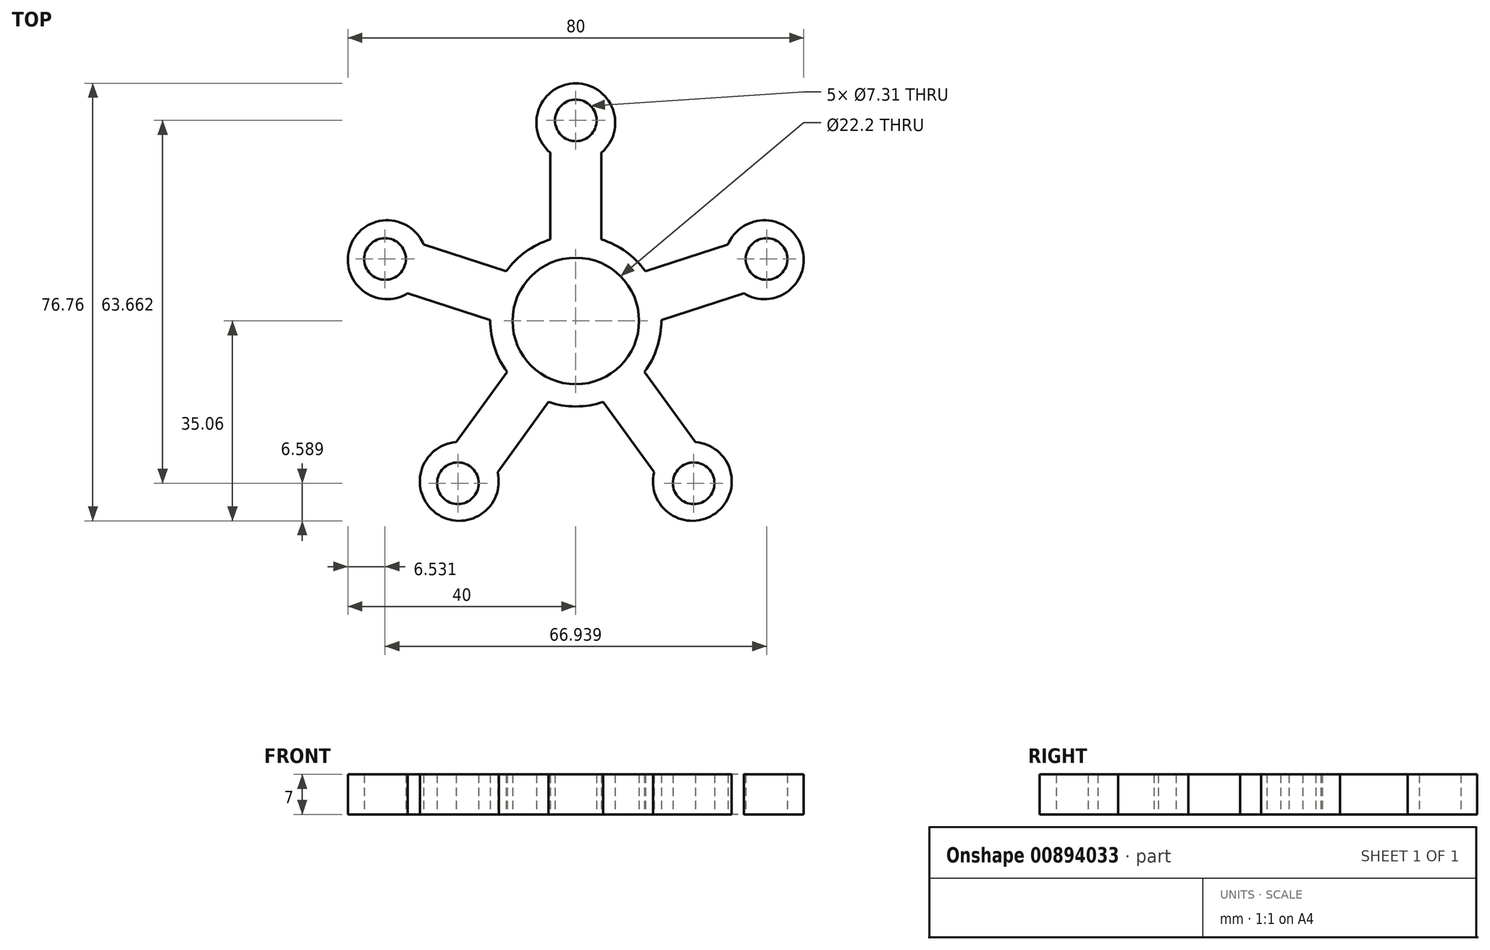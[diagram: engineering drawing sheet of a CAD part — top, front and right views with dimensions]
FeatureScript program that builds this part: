
annotation { "Feature Type Name" : "Feature", "Feature Type Description" : "" }
export const myFeature = defineFeature(function(context is Context, id is Id, definition is map)
    precondition{}
    {
        {
            var Q0;
            Q0=qCreatedBy(makeId("Top.planeOp"),FACE);
            var sketch = newSketch(context, id + "F0", { "sketchPlane" : qUnion([Q0])});
            skCircle(sketch, "E0", {"center": v(0, 0) * mm, "radius": 11.1 * mm});
            skSolve(sketch);
        }
        {
            var Q0;
            Q0=qCreatedBy(makeId("Top.planeOp"),FACE);
            var sketch = newSketch(context, id + "F1", { "sketchPlane" : qUnion([Q0])});
            skArc(sketch, "E1", {"start": v(-4.5, 14.3) * mm, "mid": v(-8.82, 12.14) * mm, "end": v(-12.22, 8.7) * mm});
            skLineSegment(sketch, "E2", {"start": v(-4.5, 14.3) * mm, "end": v(-4.5, 29.53) * mm});
            skLineSegment(sketch, "E3.MirrorCS", {"start": v(4.5, 14.3) * mm, "end": v(4.5, 29.53) * mm});
            skArc(sketch, "E4", {"start": v(4.5, 29.53) * mm, "mid": v(0, 41.7) * mm, "end": v(-4.5, 29.53) * mm});
            skPoint(sketch, "E4.third.point", {"position": v(4.5, 40.04) * mm});
            skArc(sketch, "E5.1.0", {"start": v(-26.7, 13.4) * mm, "mid": v(-39.66, 12.89) * mm, "end": v(-29.47, 4.85) * mm});
            skLineSegment(sketch, "E5.1.1", {"start": v(-12.22, 8.7) * mm, "end": v(-26.7, 13.4) * mm});
            skLineSegment(sketch, "E5.1.2", {"start": v(-15, 0.14) * mm, "end": v(-29.47, 4.85) * mm});
            skArc(sketch, "E5.2.0", {"start": v(-21, -21.24) * mm, "mid": v(-24.51, -33.74) * mm, "end": v(-13.72, -26.53) * mm});
            skLineSegment(sketch, "E5.2.1", {"start": v(-12.05, -8.93) * mm, "end": v(-21, -21.24) * mm});
            skLineSegment(sketch, "E5.2.2", {"start": v(-4.77, -14.22) * mm, "end": v(-13.72, -26.53) * mm});
            skArc(sketch, "E5.3.0", {"start": v(13.72, -26.53) * mm, "mid": v(24.51, -33.74) * mm, "end": v(21, -21.24) * mm});
            skLineSegment(sketch, "E5.3.1", {"start": v(4.77, -14.22) * mm, "end": v(13.72, -26.53) * mm});
            skLineSegment(sketch, "E5.3.2", {"start": v(12.05, -8.93) * mm, "end": v(21, -21.24) * mm});
            skArc(sketch, "E5.4.0", {"start": v(29.47, 4.85) * mm, "mid": v(39.66, 12.89) * mm, "end": v(26.7, 13.4) * mm});
            skLineSegment(sketch, "E5.4.1", {"start": v(15, 0.14) * mm, "end": v(29.47, 4.85) * mm});
            skLineSegment(sketch, "E5.4.2", {"start": v(12.22, 8.7) * mm, "end": v(26.7, 13.4) * mm});
            skArc(sketch, "E6.trimOffspring", {"start": v(12.22, 8.7) * mm, "mid": v(8.82, 12.14) * mm, "end": v(4.5, 14.3) * mm});
            skArc(sketch, "E7.trimOffspring", {"start": v(-15, 0.14) * mm, "mid": v(-14.27, -4.64) * mm, "end": v(-12.05, -8.93) * mm});
            skArc(sketch, "E8.trimOffspring", {"start": v(-4.77, -14.22) * mm, "mid": v(0, -15) * mm, "end": v(4.77, -14.22) * mm});
            skArc(sketch, "E9.trimOffspring", {"start": v(12.05, -8.93) * mm, "mid": v(14.27, -4.64) * mm, "end": v(15, 0.14) * mm});
            skSolve(sketch);
        }
        {
            var Q0;
            Q0 = qSketchRegion(id + "F1", true);
            extrude(context, id + "F2", {"entities" : qUnion([Q0]), "depth" : 7 * mm, "offsetDistance" : 25 * mm});
        }
        {
            var Q0;
            Q0 = qSketchRegion(id + "F0", true);
            extrude(context, id + "F3", {"entities" : qUnion([Q0]), "operationType" : NewBodyOperationType.REMOVE, "endBound" : BoundingType.THROUGH_ALL, "depth" : 7.1 * mm, "offsetDistance" : 25 * mm});
        }
        {
            var Q0;
            Q0=qCreatedBy(makeId("Top.planeOp"),FACE);
            var sketch = newSketch(context, id + "F4", { "sketchPlane" : qUnion([Q0])});
            skCircle(sketch, "E10", {"center": v(0, 35.2) * mm, "radius": 3.65 * mm});
            skCircle(sketch, "E11.1.0", {"center": v(-33.47, 10.87) * mm, "radius": 3.65 * mm});
            skCircle(sketch, "E11.2.0", {"center": v(-20.69, -28.47) * mm, "radius": 3.65 * mm});
            skCircle(sketch, "E11.3.0", {"center": v(20.69, -28.47) * mm, "radius": 3.65 * mm});
            skCircle(sketch, "E11.4.0", {"center": v(33.47, 10.87) * mm, "radius": 3.65 * mm});
            skPoint(sketch, "E11.center", {"position": v(0, 0) * mm});
            skSolve(sketch);
        }
        {
            var Q0;
            Q0 = qSketchRegion(id + "F4", true);
            extrude(context, id + "F5", {"entities" : qUnion([Q0]), "operationType" : NewBodyOperationType.REMOVE, "endBound" : BoundingType.THROUGH_ALL, "depth" : 25 * mm, "offsetDistance" : 25 * mm});
        }
    });
